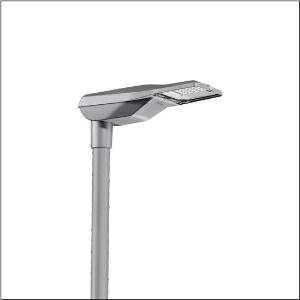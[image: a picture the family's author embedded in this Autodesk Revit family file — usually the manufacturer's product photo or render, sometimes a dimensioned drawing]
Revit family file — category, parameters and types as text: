
# Revit family: streetlight_sl_21_iq_micro___st1_0a_5xe1d61g08cb_d415
name_source: partatom
category: Lighting Fixtures
units: mm (PartAtom-declared; Revit-internal decimal feet)

## family parameters
Cut with Voids When Loaded = No
Host = Face
Light Source = No
Part Type = Normal
Room Calculation Point = No
Round Connector Dimension = Use Diameter
Shared = No

## types (1)
- --- (1 x LED, 2570 lm, 19.4 W, 2700K)
    Apparent Load = 19 VA
    CIE Flux Codes = 37 72 97 100 100
    Color Rendering = 70
    Color Temperature = 2700K
    Default Elevation = 1800 mm
    Description = Streetlight SL 21 iQ micro, mast luminaire, primary light control with lens, of PMMA, primary optical cover: cover, of toughened safety glass, transparent, light distribution: ST1.0a, light emission: direct distribution, primary light characteristic: asymmetric, installation type: post-top, side-entry, LED, High Power LED, rated luminous flux: 2.570lm, luminous efficacy: 133lm/W, light colour: 727, colour temperature: 2700K, control gear: iQ Street-Remote, control: Street-Remote, Auto-Match, Temp-Guard, Lumen-Switch, Night-Set, Smart-Wire, Light-Fading, Desk-Remote (wireless, voltage-free reading and setting of iQ features in the workshop via application-optimized NFC function/RFID function), optimised constant luminous flux control (CLO 2.0), pre-setting: linear dimming characteristic, mains connection: 220..240V, AC, 50/60Hz, start of lifetime: 19W, end of service life: 20W, reduction: 10W, luminaire housing, of diecast aluminium, powder-coated, Siteco® metallic grey (DB 702S), corrosivity category C5 high according to DIN EN ISO 12944, please order mast flange separately, inclination adjustable: 0°, 5°, 10°, 15°, sealing non-destructively replaceable, multi-level sealing system, length: 528mm, width: 235mm, height: 110mm, mast flange for spigot size: 42mm (side-entry): 5XC10008XM4, 60/48mm (side-entry/post-top): 5XC10108XM2, 76/60mm (side-entry/post-top): 5XC10108XM1, protection rating (complete): IP66, insulation class (complete): insulation class II (safety insulation), certification: CE, ENEC, ENEC+, VDE, impact resistance: IK10, permissible operating ambient temperature for outdoor applications: -40..+50°C, standard-compliant lighting for roads and squares, packaging unit: 1 piece

Light Distribution: ST1.0a
    Height = 110 mm
    Lamp = 1 x LED
    Lamp Light Flux = 2570 lm
    Lamp Power = 19.4 W
    Lamp count = 1
    Length = 528 mm
    Luminous efficacy = 132 lm/W
    Manufacturer = Siteco
    ModVariant = No
    Model = 5XE1D61G08CB
    Number of Poles = 1
    OnlyDefault = Yes
    Power Factor = 1
    Product Name = Streetlight SL 21 iQ micro | ST1.0a
    Product group = mast luminaire | pylon top
    ProductGroupID = 6100
    Protection Class = Protection class II
    Protection Degree = IP 66
    RLX_Detail_Level = 1
    RLX_Emergency_Light_Flux = 0 lm
    RLX_Emergency_Type = 0
    RLX_Emergency_Type_DB = No
    RlxData = <blob elided: 98617 chars, md5=2a16c2d8>
    Socket = socket
    Standby Power = 0 W
    System Light Flux = 2570 lm
    System Power = 19 W
    Type Comments = factory setting: luminous flux: 100 % | dim-lin: 254 | 387 mA
    Type Image = l_1006881.jpg
    URL = http://relux.com
    VarID = @adj_142385
    Voltage = 0 V
    Weight = 0.00 kg
    Width = 235 mm

## geometry (parser evidence)
native form markers: Blend x4, Sweep x10
no freeform markers — native parametric forms only
